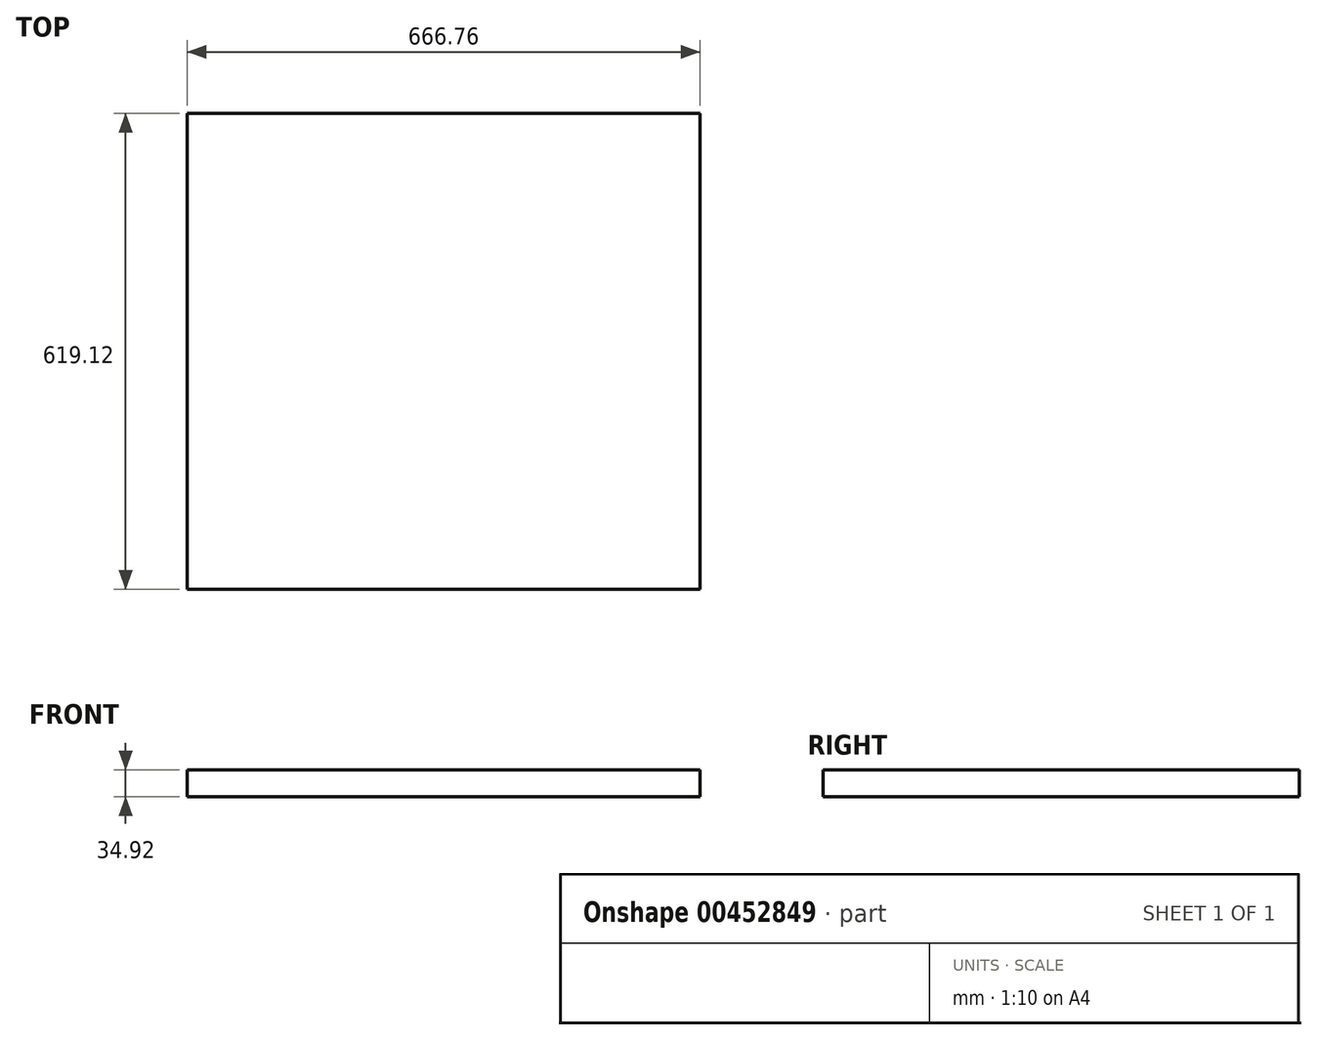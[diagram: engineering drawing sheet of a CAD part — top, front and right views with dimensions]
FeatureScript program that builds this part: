
annotation { "Feature Type Name" : "Feature", "Feature Type Description" : "" }
export const myFeature = defineFeature(function(context is Context, id is Id, definition is map)
    precondition{}
    {
        {
            var Q0;
            Q0=qCreatedBy(makeId("Top.planeOp"),FACE);
            var sketch = newSketch(context, id + "F0", { "sketchPlane" : qUnion([Q0])});
            skLineSegment(sketch, "E0.bottom", {"start": v(333.38, 309.56) * mm, "end": v(-333.38, 309.56) * mm});
            skLineSegment(sketch, "E0.top", {"start": v(333.38, -309.56) * mm, "end": v(-333.38, -309.56) * mm});
            skLineSegment(sketch, "E0.left", {"start": v(333.38, 309.56) * mm, "end": v(333.38, -309.56) * mm});
            skLineSegment(sketch, "E0.right", {"start": v(-333.38, 309.56) * mm, "end": v(-333.38, -309.56) * mm});
            skPoint(sketch, "E0.middle", {"position": v(0, 0) * mm});
            skSolve(sketch);
        }
        {
            var Q0;
            Q0 = qSketchRegion(id + "F0", true);
            extrude(context, id + "F1", {"entities" : qUnion([Q0]), "depth" : 34.92 * mm});
        }
    });
